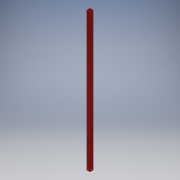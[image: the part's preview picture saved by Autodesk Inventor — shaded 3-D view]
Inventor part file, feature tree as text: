
AUTODESK INVENTOR PART (.ipt)
format: ipt  version: 2017 SP1 (Build 210196100, 196)  size: 107,520 bytes
history: native  units: in
note: dims shown in document units (in); Inventor stores cm internally (conversion verified against a paired STEP export)
features: extrude x2, sketch x2
ambient origin geometry x8: Origin, YZ Plane, XZ Plane, XY Plane, X Axis, Y Axis, Z Axis, Center Point
bodies: Solid1 (feature_tree)
feature tree (4):
  extrude  "Extrusion1"  Depth=0.0625in
  extrude  "Extrusion2"  Depth=40.0in
  sketch  "Sketch1"  dims[d0=1.0in d1=0.0625in]
  sketch  "Sketch2"  dims[d2=40.0in d3=0.0in d4=0.25in d5=0.375in d6=36.0in d7=0.0in]
